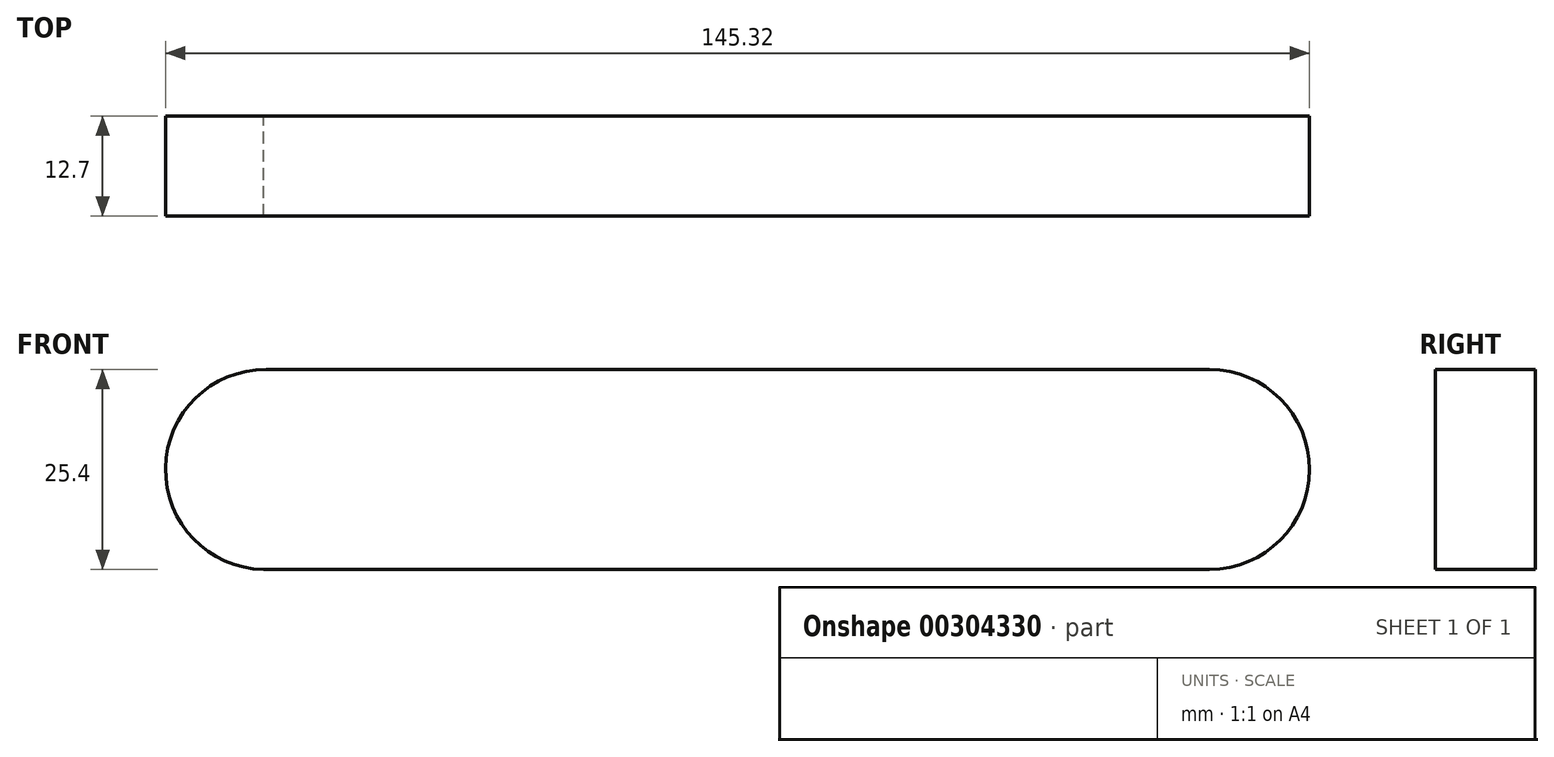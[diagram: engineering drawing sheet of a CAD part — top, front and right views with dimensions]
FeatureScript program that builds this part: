
annotation { "Feature Type Name" : "Feature", "Feature Type Description" : "" }
export const myFeature = defineFeature(function(context is Context, id is Id, definition is map)
    precondition{}
    {
        {
            var Q0;
            Q0=qCreatedBy(makeId("Front.planeOp"),FACE);
            var sketch = newSketch(context, id + "F0", { "sketchPlane" : qUnion([Q0])});
            skLineSegment(sketch, "E0.bottom", {"start": v(-38.1, 12.7) * mm, "end": v(38.1, 12.7) * mm});
            skLineSegment(sketch, "E0.top", {"start": v(-38.1, -12.7) * mm, "end": v(38.1, -12.7) * mm});
            skPoint(sketch, "E0.middle", {"position": v(0, 0) * mm});
            skArc(sketch, "E1", {"start": v(-66.2, 12.7) * mm, "mid": v(-78.96, -0.1) * mm, "end": v(-66, -12.7) * mm});
            skLineSegment(sketch, "E2", {"start": v(-66.2, 12.7) * mm, "end": v(-19.03, 12.7) * mm});
            skLineSegment(sketch, "E3", {"start": v(-66.53, -12.7) * mm, "end": v(-38.1, -12.7) * mm});
            skArc(sketch, "E4", {"start": v(53.65, -12.7) * mm, "mid": v(66.35, 0) * mm, "end": v(53.65, 12.7) * mm});
            skPoint(sketch, "E4.centerSnap0", {"position": v(38.1, 0) * mm});
            skLineSegment(sketch, "E5", {"start": v(38.1, -12.7) * mm, "end": v(53.65, -12.7) * mm});
            skLineSegment(sketch, "E6", {"start": v(38.1, 12.7) * mm, "end": v(53.65, 12.7) * mm});
            skSolve(sketch);
        }
        {
            var Q0;
            {var subQ7=sQuery(id+"F0.wireOp",EDGE,"E0.top");Q0=makeQuery(id+"F0.imprint","IMPRINT",FACE,{"disambiguationData":[TD([[makeQuery(id+"F0.imprint","IMPRINT",EDGE,{"derivedFrom":subQ7}),1.0]])]});}
            extrude(context, id + "F1", {"entities" : qUnion([Q0]), "depth" : 12.7 * mm});
        }
    });
